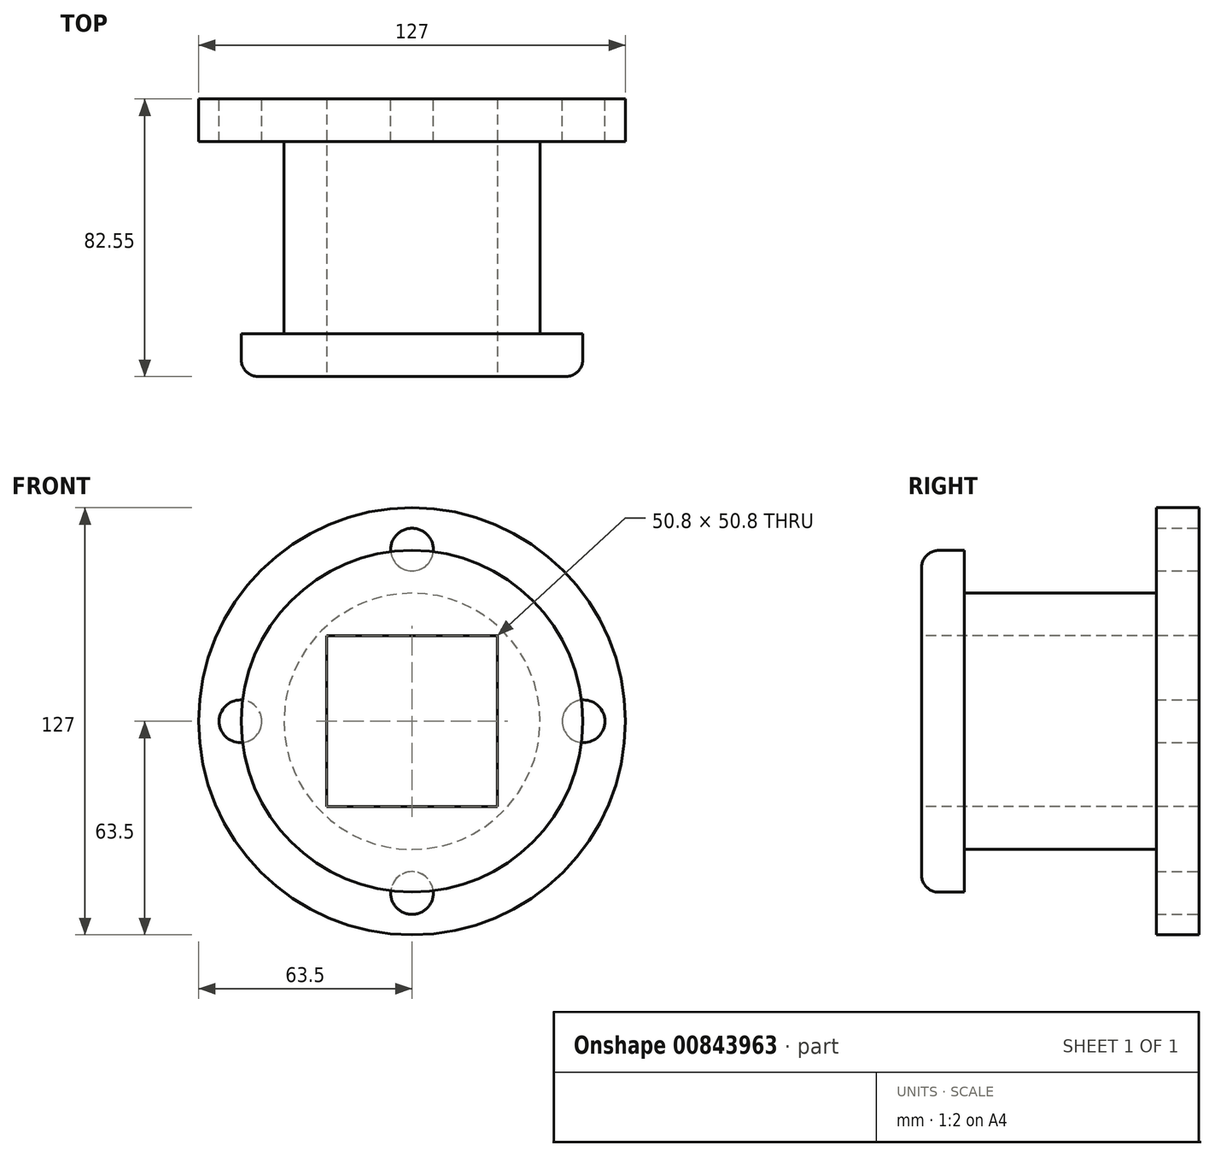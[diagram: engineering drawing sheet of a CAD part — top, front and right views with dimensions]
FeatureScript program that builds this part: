
annotation { "Feature Type Name" : "Feature", "Feature Type Description" : "" }
export const myFeature = defineFeature(function(context is Context, id is Id, definition is map)
    precondition{}
    {
        {
            var Q0;
            Q0=qCreatedBy(makeId("Front.planeOp"),FACE);
            var sketch = newSketch(context, id + "F0", { "sketchPlane" : qUnion([Q0])});
            skCircle(sketch, "E0", {"center": v(0, 0) * mm, "radius": 63.5 * mm});
            skSolve(sketch);
        }
        {
            var Q0;
            Q0 = qSketchRegion(id + "F0", true);
            extrude(context, id + "F1", {"entities" : qUnion([Q0]), "depth" : 12.7 * mm, "offsetDistance" : 25.4 * mm});
        }
        {
            var Q0;
            Q0=makeQuery(id+"F1.opExtrude","CAP_FACE",FACE,{"disambiguationData":[OSD([sQuery(id+"F0.wireOp",EDGE,"E0")])],"isStart":false});
            var sketch = newSketch(context, id + "F2", { "sketchPlane" : qUnion([Q0])});
            skCircle(sketch, "E1", {"center": v(0, 0) * mm, "radius": 38.1 * mm});
            skSolve(sketch);
        }
        {
            var Q0;
            Q0=makeQuery(id+"F2.imprint","IMPRINT",FACE,{"disambiguationData":[TD([[makeQuery(id+"F2.imprint","IMPRINT",EDGE,{"derivedFrom":sQuery(id+"F2.wireOp",EDGE,"E1")}),1.0]])]});
            extrude(context, id + "F3", {"entities" : qUnion([Q0]), "operationType" : NewBodyOperationType.ADD, "depth" : 57.15 * mm, "offsetDistance" : 25.4 * mm});
        }
        {
            var Q0;
            Q0=makeQuery(id+"F3.opExtrude","CAP_FACE",FACE,{"disambiguationData":[OSD([sQuery(id+"F2.wireOp",EDGE,"E1")])],"isStart":false});
            var sketch = newSketch(context, id + "F4", { "sketchPlane" : qUnion([Q0])});
            skCircle(sketch, "E2", {"center": v(0, 0) * mm, "radius": 50.8 * mm});
            skSolve(sketch);
        }
        {
            var Q0;
            Q0=makeQuery(id+"F1.opExtrude","CAP_FACE",FACE,{"disambiguationData":[OSD([sQuery(id+"F0.wireOp",EDGE,"E0")])],"isStart":true});
            var sketch = newSketch(context, id + "F5", { "sketchPlane" : qUnion([Q0])});
            skCircle(sketch, "E3", {"center": v(0, 51.05) * mm, "radius": 6.35 * mm});
            skCircle(sketch, "E4.1.0", {"center": v(-51.05, 0) * mm, "radius": 6.35 * mm});
            skCircle(sketch, "E4.2.0", {"center": v(0, -51.05) * mm, "radius": 6.35 * mm});
            skCircle(sketch, "E4.3.0", {"center": v(51.05, 0) * mm, "radius": 6.35 * mm});
            skPoint(sketch, "E4.center", {"position": v(0, 0) * mm});
            skSolve(sketch);
        }
        {
            var Q0;
            Q0 = qSketchRegion(id + "F5", true);
            extrude(context, id + "F6", {"entities" : qUnion([Q0]), "operationType" : NewBodyOperationType.REMOVE, "oppositeDirection" : true, "depth" : 25.4 * mm, "offsetDistance" : 25.4 * mm});
        }
        {
            var Q0;
            Q0=makeQuery(id+"F4.imprint","IMPRINT",FACE,{"disambiguationData":[TD([[makeQuery(id+"F4.imprint","IMPRINT",EDGE,{"derivedFrom":sQuery(id+"F4.wireOp",EDGE,"E2")}),1.0]])]});
            var Q1;
            Q1=makeQuery(id+"F4.imprint","IMPRINT",FACE,{"disambiguationData":[TD([[makeQuery(id+"F4.imprint","IMPRINT",EDGE,{"derivedFrom":makeQuery(id+"F3.opExtrude","CAP_EDGE",EDGE,{"disambiguationData":[OSD([sQuery(id+"F2.wireOp",EDGE,"E1")])],"isStart":false})}),1.0]])]});
            extrude(context, id + "F7", {"entities" : qUnion([Q0, Q1]), "operationType" : NewBodyOperationType.ADD, "depth" : 12.7 * mm, "offsetDistance" : 25.4 * mm});
        }
        {
            var Q0;
            Q0=makeQuery(id+"F7.opExtrude","CAP_FACE",FACE,{"disambiguationData":[OSD([sQuery(id+"F4.wireOp",EDGE,"E2")])],"isStart":false});
            var sketch = newSketch(context, id + "F8", { "sketchPlane" : qUnion([Q0])});
            skLineSegment(sketch, "E5.bottom", {"start": v(-25.4, 25.4) * mm, "end": v(25.4, 25.4) * mm});
            skLineSegment(sketch, "E5.top", {"start": v(-25.4, -25.4) * mm, "end": v(25.4, -25.4) * mm});
            skLineSegment(sketch, "E5.left", {"start": v(-25.4, 25.4) * mm, "end": v(-25.4, -25.4) * mm});
            skLineSegment(sketch, "E5.right", {"start": v(25.4, 25.4) * mm, "end": v(25.4, -25.4) * mm});
            skSolve(sketch);
        }
        {
            var Q0;
            Q0=makeQuery(id+"F7.opExtrude","CAP_FACE",FACE,{"disambiguationData":[OSD([sQuery(id+"F4.wireOp",EDGE,"E2")])],"isStart":false});
            fillet(context, id + "F9", {"entities" : qUnion([Q0]), "radius" : 5.08 * mm, "tangentPropagation" : true, "allowEdgeOverflow" : false});
        }
        {
            var Q0;
            Q0=makeQuery(id+"F8.imprint","IMPRINT",FACE,{"disambiguationData":[TD([[makeQuery(id+"F8.imprint","IMPRINT",EDGE,{"derivedFrom":sQuery(id+"F8.wireOp",EDGE,"E5.bottom")}),-1.0]])]});
            extrude(context, id + "F10", {"entities" : qUnion([Q0]), "operationType" : NewBodyOperationType.REMOVE, "oppositeDirection" : true, "depth" : 127 * mm, "offsetDistance" : 25.4 * mm});
        }
    });
